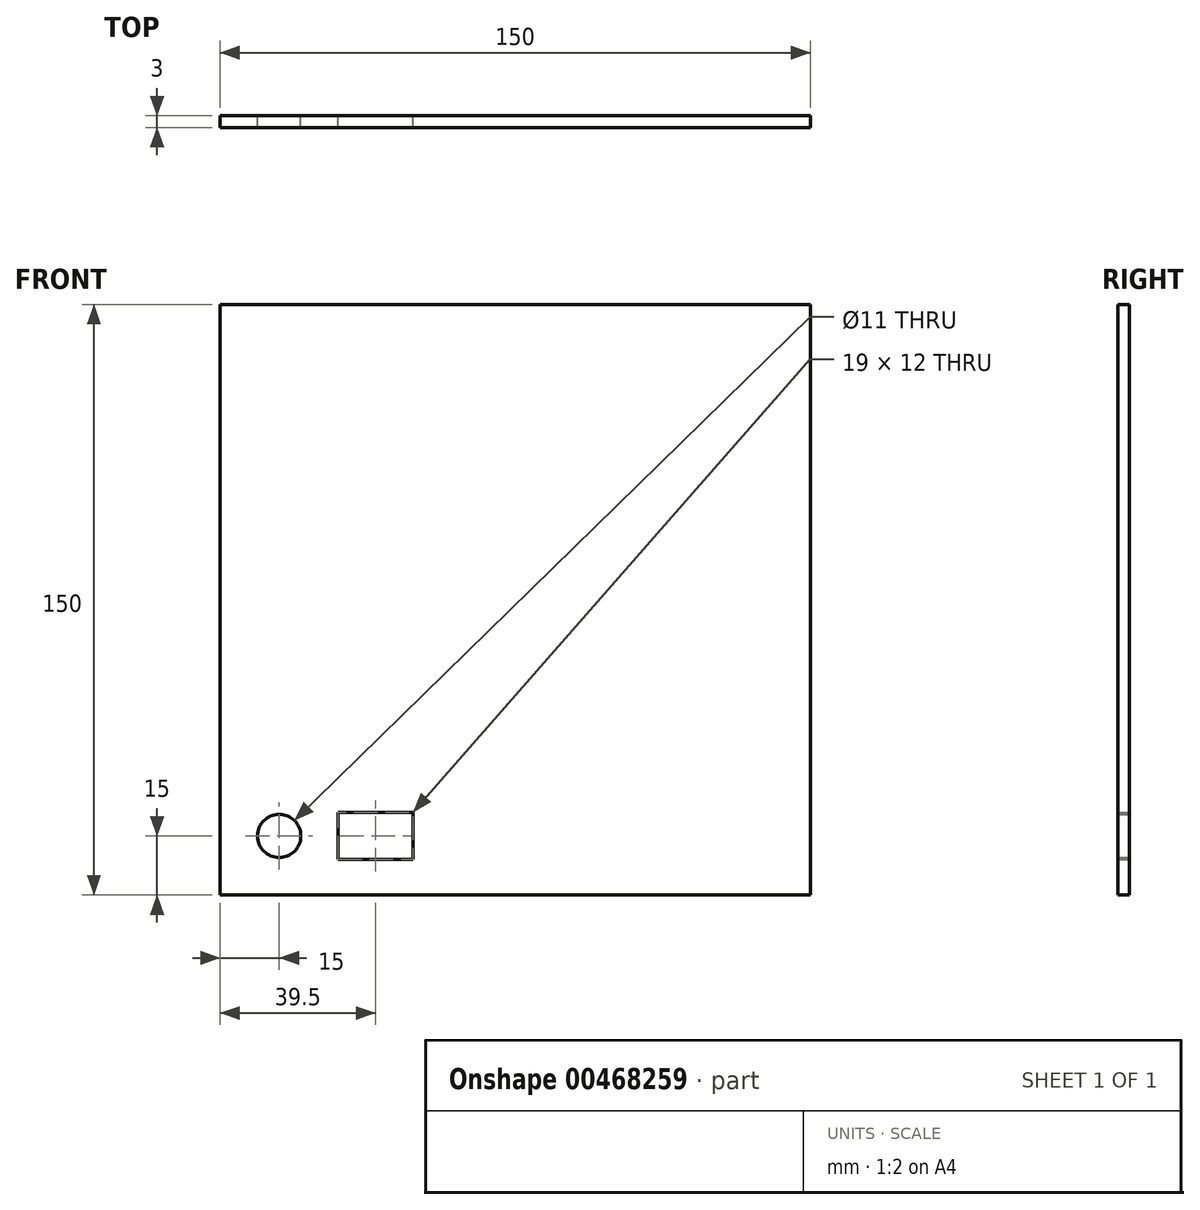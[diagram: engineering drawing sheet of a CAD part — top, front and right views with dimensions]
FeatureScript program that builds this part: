
annotation { "Feature Type Name" : "Feature", "Feature Type Description" : "" }
export const myFeature = defineFeature(function(context is Context, id is Id, definition is map)
    precondition{}
    {
        {
            var Q0;
            Q0=qCreatedBy(makeId("Front.planeOp"),FACE);
            var sketch = newSketch(context, id + "F0", { "sketchPlane" : qUnion([Q0])});
            skLineSegment(sketch, "E0.bottom", {"start": v(75, -75) * mm, "end": v(-75, -75) * mm});
            skLineSegment(sketch, "E0.top", {"start": v(75, 75) * mm, "end": v(-75, 75) * mm});
            skLineSegment(sketch, "E0.left", {"start": v(75, -75) * mm, "end": v(75, 75) * mm});
            skLineSegment(sketch, "E0.right", {"start": v(-75, -75) * mm, "end": v(-75, 75) * mm});
            skPoint(sketch, "E0.middle", {"position": v(0, 0) * mm});
            skCircle(sketch, "E1", {"center": v(-60, -60) * mm, "radius": 5.5 * mm});
            skLineSegment(sketch, "E2.bottom", {"start": v(-26, -66) * mm, "end": v(-45, -66) * mm});
            skLineSegment(sketch, "E2.top", {"start": v(-26, -54) * mm, "end": v(-45, -54) * mm});
            skLineSegment(sketch, "E2.left", {"start": v(-26, -66) * mm, "end": v(-26, -54) * mm});
            skLineSegment(sketch, "E2.right", {"start": v(-45, -66) * mm, "end": v(-45, -54) * mm});
            skPoint(sketch, "E2.middle", {"position": v(-35.5, -60) * mm});
            skSolve(sketch);
        }
        {
            var Q0;
            Q0 = qSketchRegion(id + "F0", true);
            extrude(context, id + "F1", {"entities" : qUnion([Q0]), "depth" : 3 * mm});
        }
    });
